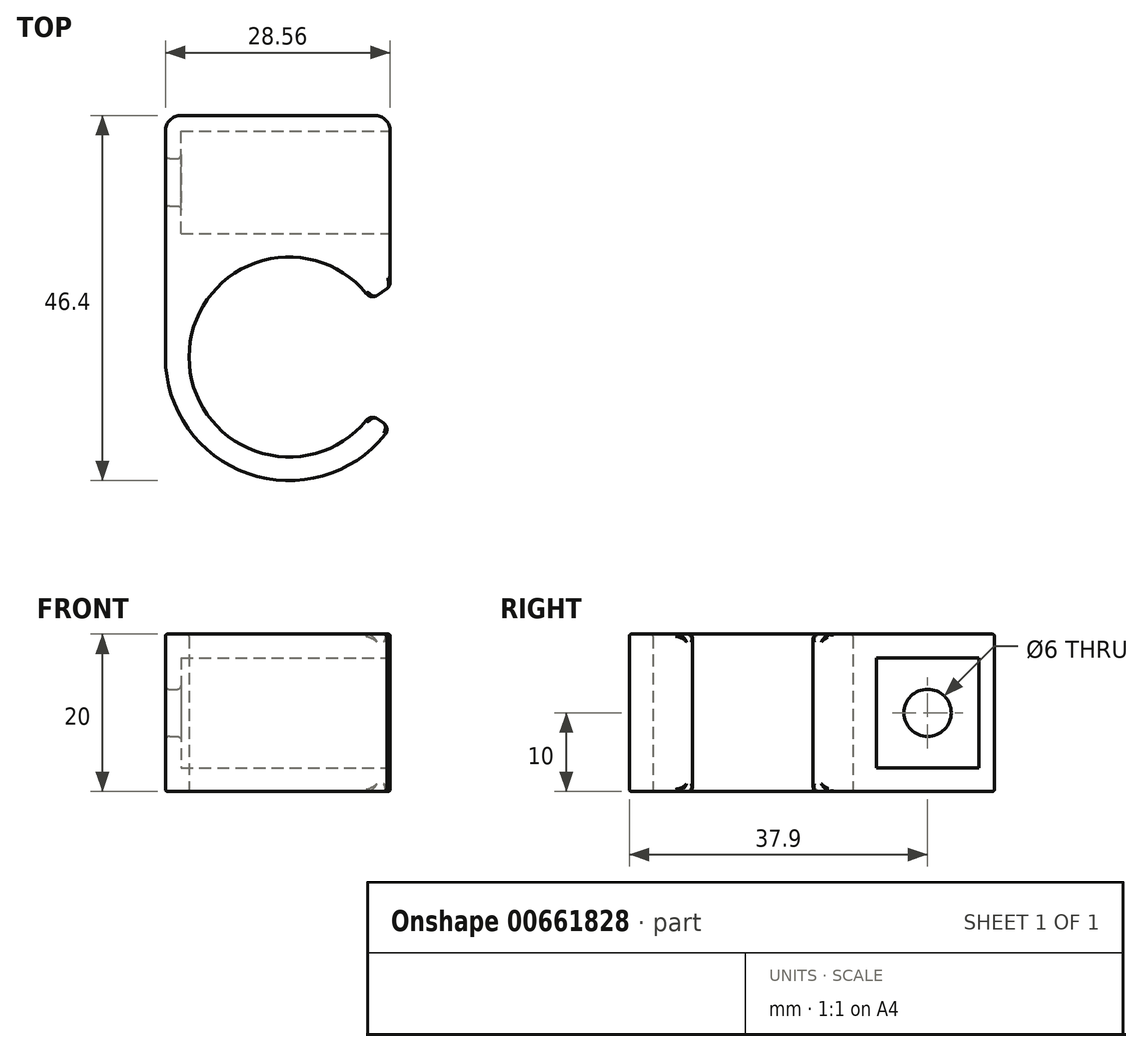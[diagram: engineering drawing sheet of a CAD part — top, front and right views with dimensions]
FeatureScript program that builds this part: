
annotation { "Feature Type Name" : "Feature", "Feature Type Description" : "" }
export const myFeature = defineFeature(function(context is Context, id is Id, definition is map)
    precondition{}
    {
        {
            var Q0;
            Q0=qCreatedBy(makeId("Top.planeOp"),FACE);
            var sketch = newSketch(context, id + "F0", { "sketchPlane" : qUnion([Q0])});
            skCircle(sketch, "E0", {"center": v(0, 0) * mm, "radius": 12.7 * mm});
            skCircle(sketch, "E1.0", {"center": v(0, 0) * mm, "radius": 15.7 * mm});
            skLineSegment(sketch, "E2", {"start": v(0, 0) * mm, "end": v(21.2, 14.85) * mm});
            skLineSegment(sketch, "E3", {"start": v(0, 0) * mm, "end": v(26.1, -18.28) * mm});
            skLineSegment(sketch, "E4", {"start": v(-15.7, 0) * mm, "end": v(-15.7, 28.7) * mm});
            skLineSegment(sketch, "E5", {"start": v(-13.7, 30.7) * mm, "end": v(10.86, 30.7) * mm});
            skLineSegment(sketch, "E6", {"start": v(12.86, 28.7) * mm, "end": v(12.86, 9) * mm});
            skLineSegment(sketch, "E7.0", {"start": v(-13.7, 28.7) * mm, "end": v(12.86, 28.7) * mm});
            skLineSegment(sketch, "E7.1", {"start": v(-13.7, 0) * mm, "end": v(-13.7, 28.7) * mm});
            skLineSegment(sketch, "E8", {"start": v(-13.7, 15.7) * mm, "end": v(12.86, 15.7) * mm});
            skPoint(sketch, "E9.visualSharp", {"position": v(-15.7, 30.7) * mm});
            skArc(sketch, "E9.filletArc", {"start": v(-13.7, 30.7) * mm, "mid": v(-15.11, 30.11) * mm, "end": v(-15.7, 28.7) * mm});
            skPoint(sketch, "E10.visualSharp", {"position": v(12.86, 30.7) * mm});
            skArc(sketch, "E10.filletArc", {"start": v(12.86, 28.7) * mm, "mid": v(12.27, 30.11) * mm, "end": v(10.86, 30.7) * mm});
            skSolve(sketch);
        }
        {
            var Q0;
            {var subQ0=sQuery(id+"F0.wireOp",EDGE,"E6");var subQ3=sQuery(id+"F0.wireOp",EDGE,"E8");var subQ5=makeQuery(id+"F0.imprint","INTERSECT",VERTEX,{"derivedFrom":[subQ0,subQ3]});Q0=makeQuery(id+"F0.imprint","IMPRINT",FACE,{"disambiguationData":[TD([[makeQuery(id+"F0.imprint","IMPRINT",EDGE,{"disambiguationData":[TD([[subQ5,1.0]])],"derivedFrom":subQ3}),-1.0]])]});}
            var Q1;
            {var subQ1=sQuery(id+"F0.wireOp",EDGE,"E4");Q1=makeQuery(id+"F0.imprint","IMPRINT",FACE,{"disambiguationData":[TD([[makeQuery(id+"F0.imprint","IMPRINT",EDGE,{"derivedFrom":subQ1}),-1.0]])]});}
            var Q2;
            {var subQ4=sQuery(id+"F0.wireOp",EDGE,"E7.0");Q2=makeQuery(id+"F0.imprint","IMPRINT",FACE,{"disambiguationData":[TD([[makeQuery(id+"F0.imprint","IMPRINT",EDGE,{"derivedFrom":subQ4}),-1.0]])]});}
            var Q3;
            {var subQ0=sQuery(id+"F0.wireOp",EDGE,"E8");var subQ1=sQuery(id+"F0.wireOp",EDGE,"E1.0");var subQ2=makeQuery(id+"F0.imprint","INTERSECT",VERTEX,{"derivedFrom":[subQ1,subQ0]});Q3=makeQuery(id+"F0.imprint","IMPRINT",FACE,{"disambiguationData":[TD([[makeQuery(id+"F0.imprint","IMPRINT",EDGE,{"disambiguationData":[TD([[subQ2,-1.0]])],"derivedFrom":subQ1}),-1.0]])]});}
            var Q4;
            {var subQ4=sQuery(id+"F0.wireOp",EDGE,"E2");var subQ6=sQuery(id+"F0.wireOp",EDGE,"E0");var subQ7=makeQuery(id+"F0.imprint","INTERSECT",VERTEX,{"derivedFrom":[subQ6,subQ4]});Q4=makeQuery(id+"F0.imprint","IMPRINT",FACE,{"disambiguationData":[TD([[makeQuery(id+"F0.imprint","IMPRINT",EDGE,{"disambiguationData":[TD([[subQ7,-1.0]])],"derivedFrom":subQ6}),-1.0]])]});}
            extrude(context, id + "F1", {"entities" : qUnion([Q0, Q1, Q2, Q3, Q4]), "depth" : 10 * mm, "offsetDistance" : 25 * mm, "hasSecondDirection" : true, "secondDirectionOppositeDirection" : true, "secondDirectionDepth" : 10 * mm});
        }
        {
            var Q0;
            {var subQ1=sQuery(id+"F0.wireOp",EDGE,"E7.0");Q0=makeQuery(id+"F0.imprint","IMPRINT",FACE,{"disambiguationData":[TD([[makeQuery(id+"F0.imprint","IMPRINT",EDGE,{"derivedFrom":subQ1}),-1.0]])]});}
            extrude(context, id + "F2", {"entities" : qUnion([Q0]), "operationType" : NewBodyOperationType.REMOVE, "depth" : 7 * mm, "offsetDistance" : 25 * mm, "hasSecondDirection" : true, "secondDirectionOppositeDirection" : true, "secondDirectionDepth" : 7 * mm});
        }
        {
            var Q0;
            Q0=makeQuery(id+"F2.boolean.opBoolean","COPY",FACE,{"derivedFrom":makeQuery(id+"F2.opExtrude","SWEPT_FACE",FACE,{"disambiguationData":[OSD([sQuery(id+"F0.wireOp",EDGE,"E7.1")])]})});
            var sketch = newSketch(context, id + "F3", { "sketchPlane" : qUnion([Q0])});
            skLineSegment(sketch, "E11", {"start": v(28.7, 0) * mm, "end": v(15.7, 0) * mm, "construction": true});
            skLineSegment(sketch, "E12", {"start": v(22.2, 7) * mm, "end": v(22.2, -7) * mm, "construction": true});
            skCircle(sketch, "E13", {"center": v(22.2, 0) * mm, "radius": 3 * mm});
            skSolve(sketch);
        }
        {
            var Q0;
            Q0 = qSketchRegion(id + "F3", true);
            extrude(context, id + "F4", {"entities" : qUnion([Q0]), "operationType" : NewBodyOperationType.REMOVE, "oppositeDirection" : true, "depth" : 5.1 * mm, "offsetDistance" : 25 * mm});
        }
        {
            var Q0;
            Q0=makeQuery(id+"F1.opExtrude","SWEPT_FACE",FACE,{"disambiguationData":[OSD([sQuery(id+"F0.wireOp",EDGE,"E3")])]});
            var Q1;
            Q1=makeQuery(id+"F1.opExtrude","SWEPT_FACE",FACE,{"disambiguationData":[OSD([sQuery(id+"F0.wireOp",EDGE,"E2")])]});
            fillet(context, id + "F5", {"entities" : qUnion([Q0, Q1]), "radius" : 1 * mm, "tangentPropagation" : true, "allowEdgeOverflow" : false});
        }
        {
            var Q0;
            Q0=makeQuery(id+"F4.boolean.opBoolean","COPY",FACE,{"derivedFrom":makeQuery(id+"F4.opExtrude","SWEPT_FACE",FACE,{"disambiguationData":[OSD([sQuery(id+"F3.wireOp",EDGE,"E13")])]})});
            fillet(context, id + "F6", {"entities" : qUnion([Q0]), "radius" : 0.5 * mm, "tangentPropagation" : true, "allowEdgeOverflow" : false});
        }
        {
            var Q0;
            Q0=makeQuery(id+"F1.opExtrude","CAP_FACE",FACE,{"disambiguationData":[OSD([sQuery(id+"F0.wireOp",EDGE,"E0"),sQuery(id+"F0.wireOp",EDGE,"E1.0"),sQuery(id+"F0.wireOp",EDGE,"E2"),sQuery(id+"F0.wireOp",EDGE,"E3"),sQuery(id+"F0.wireOp",EDGE,"E4"),sQuery(id+"F0.wireOp",EDGE,"E5"),sQuery(id+"F0.wireOp",EDGE,"E6"),sQuery(id+"F0.wireOp",EDGE,"E9.filletArc"),sQuery(id+"F0.wireOp",EDGE,"E10.filletArc")])],"isStart":false});
            var Q1;
            Q1=makeQuery(id+"F1.opExtrude","CAP_FACE",FACE,{"disambiguationData":[OSD([sQuery(id+"F0.wireOp",EDGE,"E0"),sQuery(id+"F0.wireOp",EDGE,"E1.0"),sQuery(id+"F0.wireOp",EDGE,"E2"),sQuery(id+"F0.wireOp",EDGE,"E3"),sQuery(id+"F0.wireOp",EDGE,"E4"),sQuery(id+"F0.wireOp",EDGE,"E5"),sQuery(id+"F0.wireOp",EDGE,"E6"),sQuery(id+"F0.wireOp",EDGE,"E9.filletArc"),sQuery(id+"F0.wireOp",EDGE,"E10.filletArc")])],"isStart":true});
            fillet(context, id + "F7", {"entities" : qUnion([Q0, Q1]), "radius" : 0.3 * mm, "tangentPropagation" : true, "allowEdgeOverflow" : false});
        }
    });
